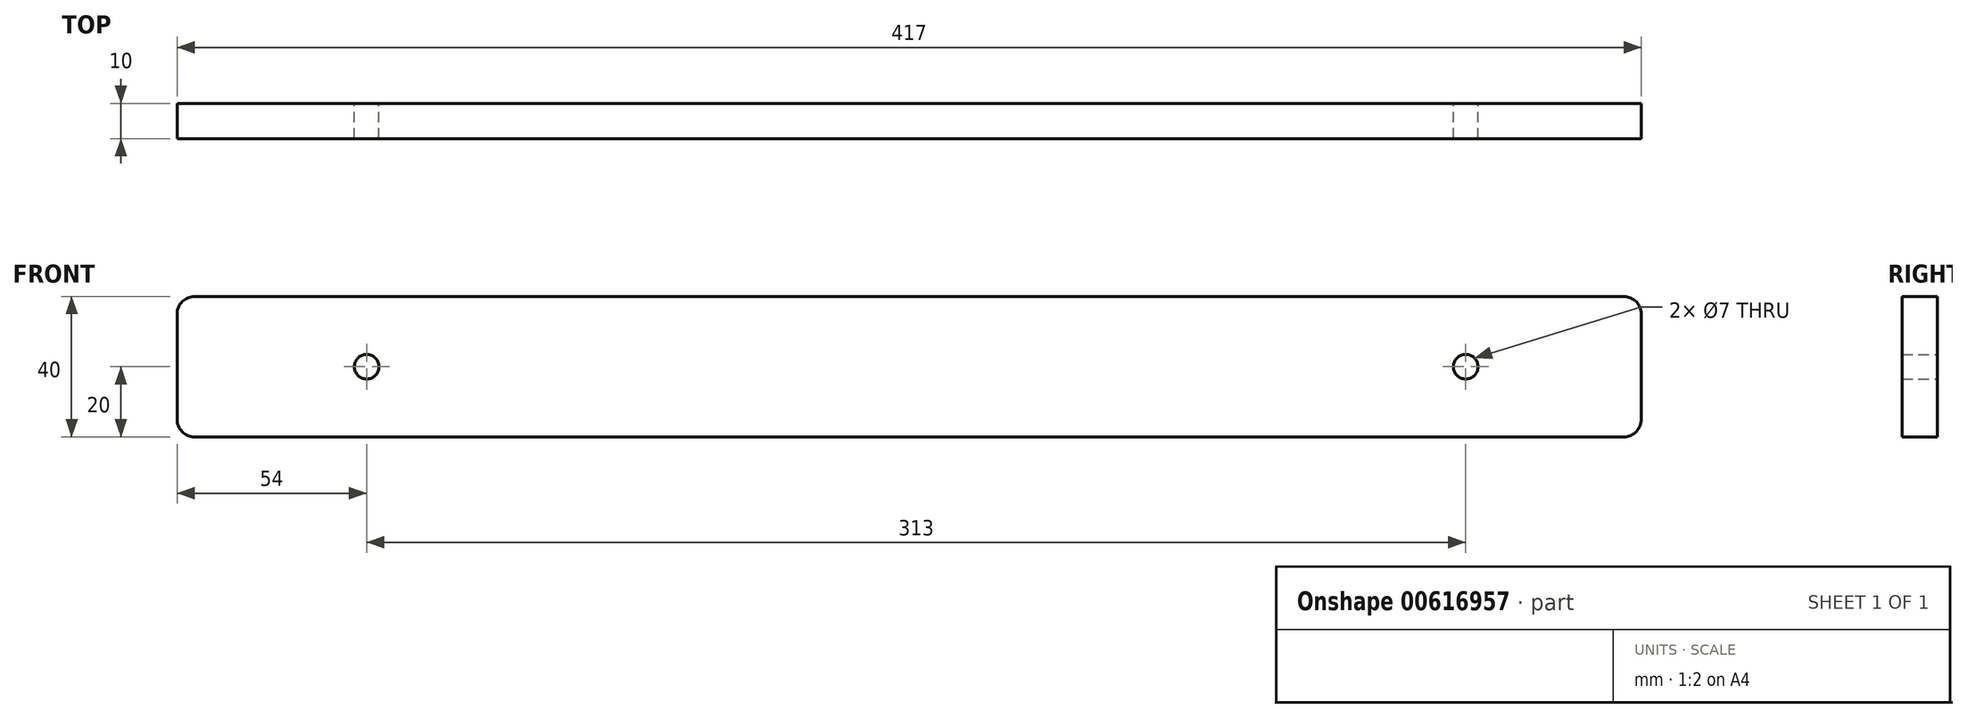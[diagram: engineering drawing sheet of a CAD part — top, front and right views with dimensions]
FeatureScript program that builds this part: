
annotation { "Feature Type Name" : "Feature", "Feature Type Description" : "" }
export const myFeature = defineFeature(function(context is Context, id is Id, definition is map)
    precondition{}
    {
        {
            var Q0;
            Q0=qCreatedBy(makeId("Front.planeOp"),FACE);
            var sketch = newSketch(context, id + "F0", { "sketchPlane" : qUnion([Q0])});
            skLineSegment(sketch, "E0.bottom", {"start": v(-203.5, 20) * mm, "end": v(203.5, 20) * mm});
            skLineSegment(sketch, "E0.top", {"start": v(-203.5, -20) * mm, "end": v(203.5, -20) * mm});
            skLineSegment(sketch, "E0.left", {"start": v(-208.5, 15) * mm, "end": v(-208.5, -15) * mm});
            skLineSegment(sketch, "E0.right", {"start": v(208.5, 15) * mm, "end": v(208.5, -15) * mm});
            skPoint(sketch, "E0.middle", {"position": v(0, 0) * mm});
            skPoint(sketch, "E1.visualSharp", {"position": v(-208.5, 20) * mm});
            skArc(sketch, "E1.filletArc", {"start": v(-203.5, 20) * mm, "mid": v(-207.04, 18.54) * mm, "end": v(-208.5, 15) * mm});
            skPoint(sketch, "E2.visualSharp", {"position": v(-208.5, -20) * mm});
            skArc(sketch, "E2.filletArc", {"start": v(-208.5, -15) * mm, "mid": v(-207.04, -18.54) * mm, "end": v(-203.5, -20) * mm});
            skPoint(sketch, "E3.visualSharp", {"position": v(208.5, -20) * mm});
            skArc(sketch, "E3.filletArc", {"start": v(203.5, -20) * mm, "mid": v(207.04, -18.54) * mm, "end": v(208.5, -15) * mm});
            skPoint(sketch, "E4.visualSharp", {"position": v(208.5, 20) * mm});
            skArc(sketch, "E4.filletArc", {"start": v(208.5, 15) * mm, "mid": v(207.04, 18.54) * mm, "end": v(203.5, 20) * mm});
            skLineSegment(sketch, "E5", {"start": v(-208.5, 0) * mm, "end": v(208.5, 0) * mm});
            skPoint(sketch, "E6", {"position": v(-154.5, 0) * mm});
            skPoint(sketch, "E7", {"position": v(158.5, 0) * mm});
            skCircle(sketch, "E8", {"center": v(-154.5, 0) * mm, "radius": 3.5 * mm});
            skCircle(sketch, "E9", {"center": v(158.5, 0) * mm, "radius": 3.5 * mm});
            skLineSegment(sketch, "E10", {"start": v(-80.5, 20) * mm, "end": v(-80.5, -20) * mm});
            skLineSegment(sketch, "E11", {"start": v(198.5, 20) * mm, "end": v(198.5, -20) * mm});
            skLineSegment(sketch, "E12", {"start": v(-70.5, 20) * mm, "end": v(-70.5, -20) * mm});
            skSolve(sketch);
        }
        {
            var Q0;
            Q0 = qSketchRegion(id + "F0", true);
            extrude(context, id + "F1", {"entities" : qUnion([Q0]), "depth" : 10 * mm, "offsetDistance" : 25 * mm});
        }
    });
